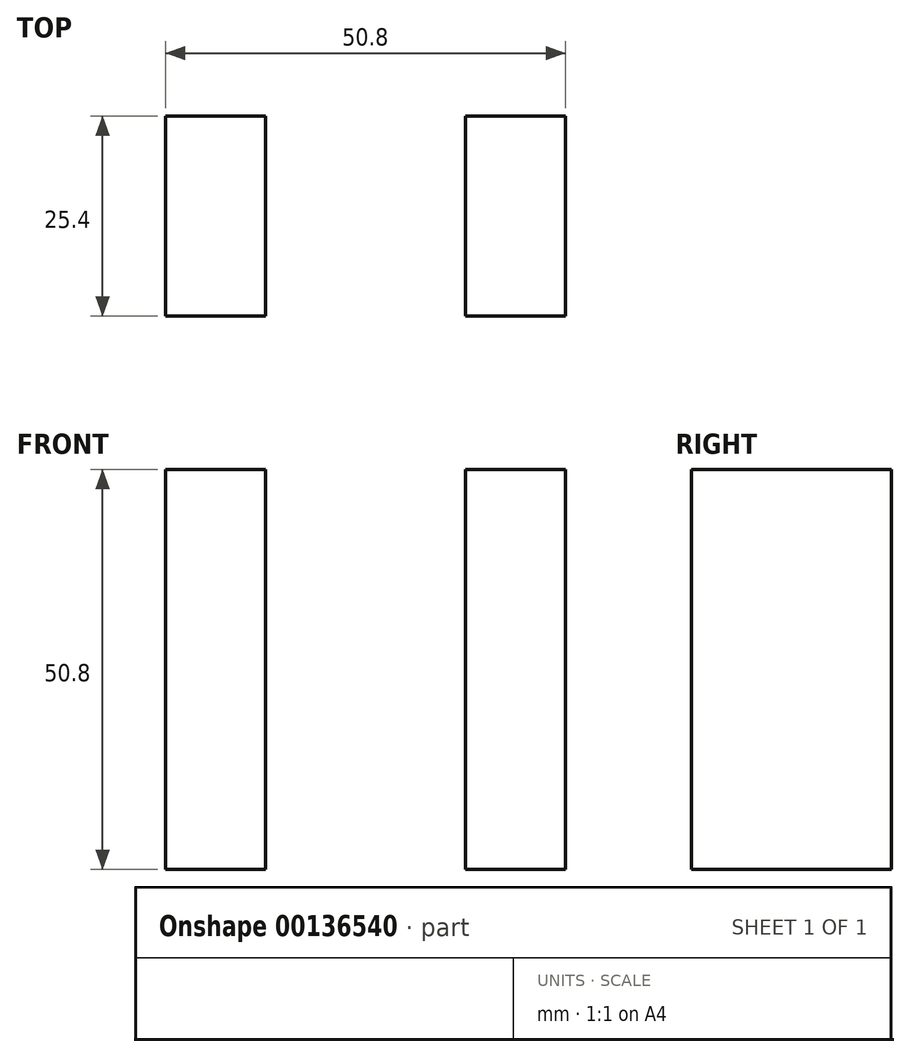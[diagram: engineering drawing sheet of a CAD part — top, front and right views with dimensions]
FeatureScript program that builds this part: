
annotation { "Feature Type Name" : "Feature", "Feature Type Description" : "" }
export const myFeature = defineFeature(function(context is Context, id is Id, definition is map)
    precondition{}
    {
        {
            var Q0;
            Q0=qCreatedBy(makeId("Front.planeOp"),FACE);
            var sketch = newSketch(context, id + "F0", { "sketchPlane" : qUnion([Q0])});
            skLineSegment(sketch, "E0.bottom", {"start": v(-12.7, 25.4) * mm, "end": v(-25.4, 25.4) * mm});
            skLineSegment(sketch, "E0.top", {"start": v(-12.7, -25.4) * mm, "end": v(-25.4, -25.4) * mm});
            skLineSegment(sketch, "E0.left", {"start": v(-12.7, 25.4) * mm, "end": v(-12.7, -25.4) * mm});
            skLineSegment(sketch, "E0.right", {"start": v(-25.4, 25.4) * mm, "end": v(-25.4, -25.4) * mm});
            skPoint(sketch, "E0.middle", {"position": v(-19.05, 0) * mm});
            skLineSegment(sketch, "E1.bottom", {"start": v(25.4, 25.4) * mm, "end": v(12.7, 25.4) * mm});
            skLineSegment(sketch, "E1.top", {"start": v(25.4, -25.4) * mm, "end": v(12.7, -25.4) * mm});
            skLineSegment(sketch, "E1.left", {"start": v(25.4, 25.4) * mm, "end": v(25.4, -25.4) * mm});
            skLineSegment(sketch, "E1.right", {"start": v(12.7, 25.4) * mm, "end": v(12.7, -25.4) * mm});
            skPoint(sketch, "E1.middle", {"position": v(19.05, 0) * mm});
            skSolve(sketch);
        }
        {
            var Q0;
            Q0 = qSketchRegion(id + "F0", true);
            extrude(context, id + "F1", {"entities" : qUnion([Q0]), "depth" : 25.4 * mm});
        }
    });
